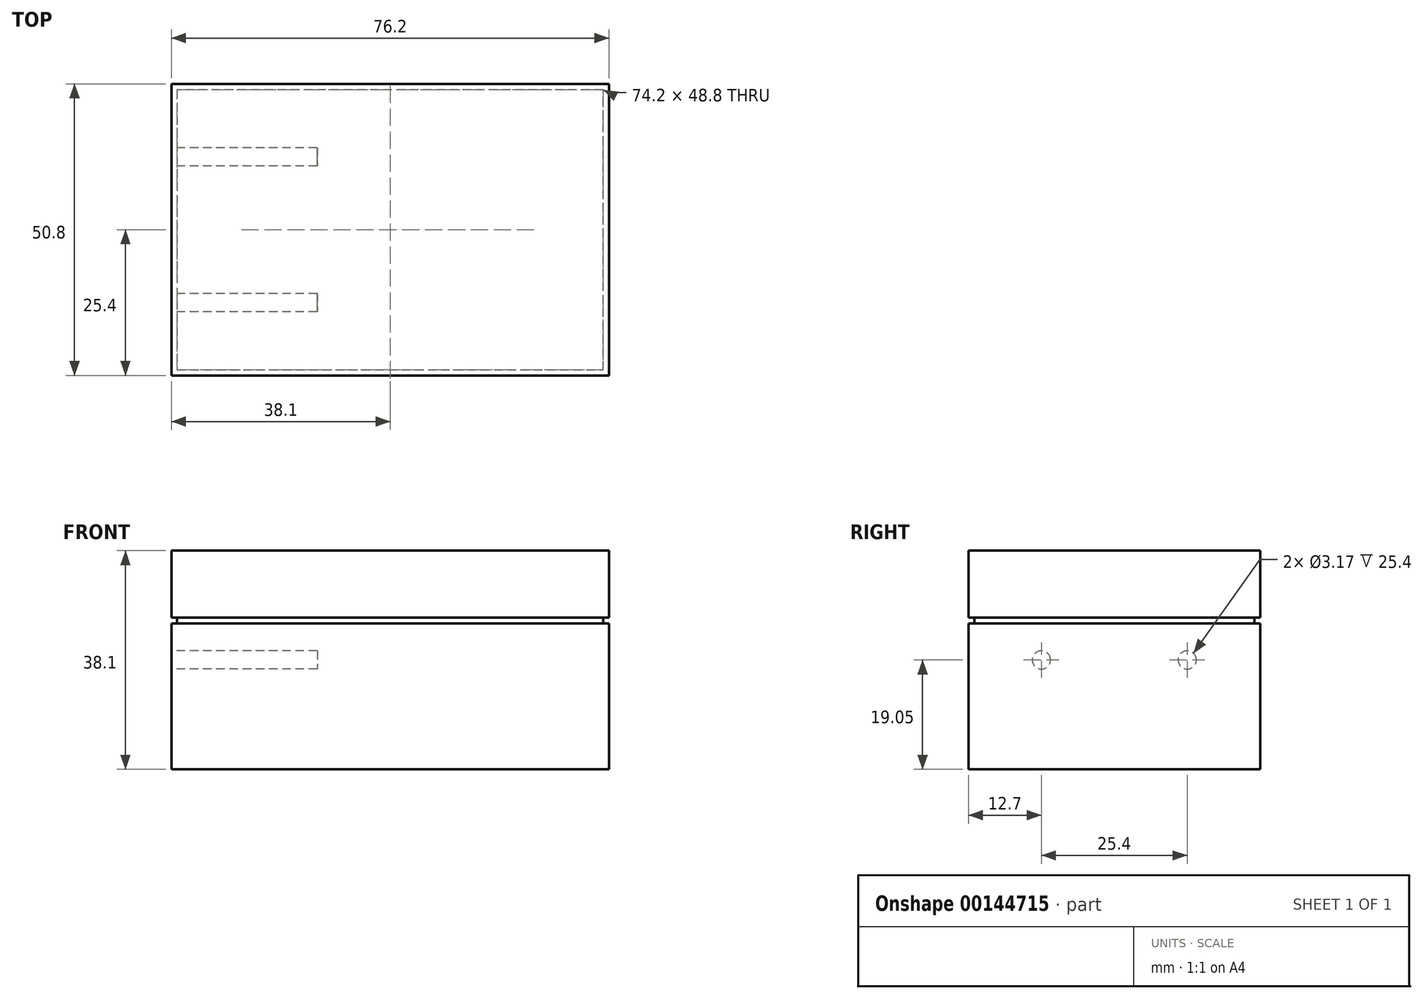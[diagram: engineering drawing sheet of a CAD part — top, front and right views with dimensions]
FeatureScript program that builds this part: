
annotation { "Feature Type Name" : "Feature", "Feature Type Description" : "" }
export const myFeature = defineFeature(function(context is Context, id is Id, definition is map)
    precondition{}
    {
        {
            var Q0;
            Q0=qCreatedBy(makeId("Top.planeOp"),FACE);
            var sketch = newSketch(context, id + "F0", { "sketchPlane" : qUnion([Q0])});
            skLineSegment(sketch, "E0.bottom", {"start": v(38.1, 25.4) * mm, "end": v(-38.1, 25.4) * mm});
            skLineSegment(sketch, "E0.top", {"start": v(38.1, -25.4) * mm, "end": v(-38.1, -25.4) * mm});
            skLineSegment(sketch, "E0.left", {"start": v(38.1, 25.4) * mm, "end": v(38.1, -25.4) * mm});
            skLineSegment(sketch, "E0.right", {"start": v(-38.1, 25.4) * mm, "end": v(-38.1, -25.4) * mm});
            skPoint(sketch, "E0.middle", {"position": v(0, 0) * mm});
            skSolve(sketch);
        }
        {
            var Q0;
            Q0 = qSketchRegion(id + "F0", true);
            extrude(context, id + "F1", {"entities" : qUnion([Q0]), "depth" : 38.1 * mm});
        }
        {
            var Q0;
            Q0=makeQuery(id+"F1.opExtrude","SWEPT_FACE",FACE,{"disambiguationData":[OSD([sQuery(id+"F0.wireOp",EDGE,"E0.right")])]});
            var sketch = newSketch(context, id + "F2", { "sketchPlane" : qUnion([Q0])});
            skLineSegment(sketch, "E1", {"start": v(-25.4, 19.05) * mm, "end": v(0, 19.05) * mm, "construction": true});
            skLineSegment(sketch, "E2", {"start": v(0, 19.05) * mm, "end": v(0, 0) * mm, "construction": true});
            skCircle(sketch, "E3", {"center": v(-12.7, 19.05) * mm, "radius": 1.59 * mm});
            skCircle(sketch, "E4", {"center": v(12.7, 19.05) * mm, "radius": 1.59 * mm});
            skPoint(sketch, "E4.centerSnap0", {"position": v(25.4, 19.05) * mm});
            skSolve(sketch);
        }
        {
            var Q0;
            Q0=qCreatedBy(makeId("Top.planeOp"),FACE);
            cPlane(context, id + "F3", {"entities" : qUnion([Q0]), "cplaneType" : CPlaneType.OFFSET, "offset" : 25.4 * mm, "width" : 152.4 * mm, "height" : 152.4 * mm});
        }
        {
            var Q0;
            Q0=qCreatedBy(id+"F3.planeOp",FACE);
            var sketch = newSketch(context, id + "F4", { "sketchPlane" : qUnion([Q0])});
            skLineSegment(sketch, "E5.0.0", {"start": v(38.1, -25.4) * mm, "end": v(38.1, 25.4) * mm});
            skLineSegment(sketch, "E5.0.1", {"start": v(38.1, 25.4) * mm, "end": v(-38.1, 25.4) * mm});
            skLineSegment(sketch, "E5.0.2", {"start": v(-38.1, 25.4) * mm, "end": v(-38.1, -25.4) * mm});
            skLineSegment(sketch, "E5.0.3", {"start": v(-38.1, -25.4) * mm, "end": v(38.1, -25.4) * mm});
            skLineSegment(sketch, "E6.0", {"start": v(37.1, -24.4) * mm, "end": v(37.1, 24.4) * mm});
            skLineSegment(sketch, "E6.1", {"start": v(-37.1, -24.4) * mm, "end": v(37.1, -24.4) * mm});
            skLineSegment(sketch, "E6.2", {"start": v(-37.1, 24.4) * mm, "end": v(-37.1, -24.4) * mm});
            skLineSegment(sketch, "E6.3", {"start": v(37.1, 24.4) * mm, "end": v(-37.1, 24.4) * mm});
            skSolve(sketch);
        }
        {
            var Q0;
            Q0 = qSketchRegion(id + "F4", true);
            extrude(context, id + "F5", {"entities" : qUnion([Q0]), "operationType" : NewBodyOperationType.REMOVE, "depth" : 1 * mm});
        }
        {
            var Q0;
            Q0 = qSketchRegion(id + "F2", true);
            extrude(context, id + "F6", {"entities" : qUnion([Q0]), "operationType" : NewBodyOperationType.REMOVE, "oppositeDirection" : true, "depth" : 25.4 * mm});
        }
    });
